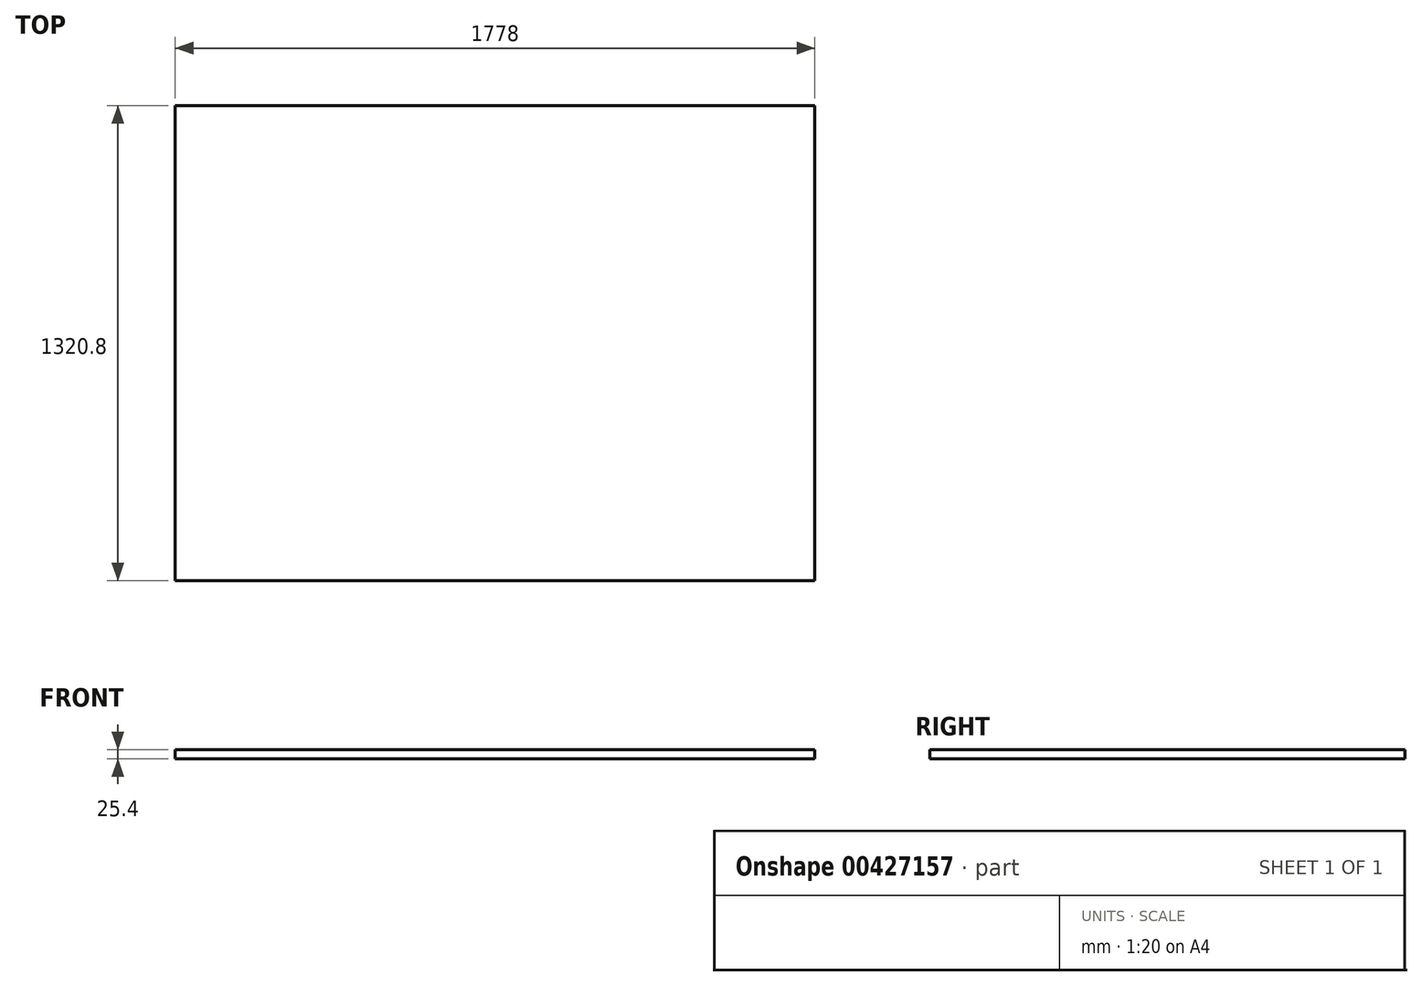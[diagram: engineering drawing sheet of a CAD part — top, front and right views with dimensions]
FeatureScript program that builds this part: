
annotation { "Feature Type Name" : "Feature", "Feature Type Description" : "" }
export const myFeature = defineFeature(function(context is Context, id is Id, definition is map)
    precondition{}
    {
        {
            var Q0;
            Q0=qCreatedBy(makeId("Top.planeOp"),FACE);
            var sketch = newSketch(context, id + "F0", { "sketchPlane" : qUnion([Q0])});
            skLineSegment(sketch, "E0.bottom", {"start": v(889, 660.4) * mm, "end": v(-889, 660.4) * mm});
            skLineSegment(sketch, "E0.top", {"start": v(889, -660.4) * mm, "end": v(-889, -660.4) * mm});
            skLineSegment(sketch, "E0.left", {"start": v(889, 660.4) * mm, "end": v(889, -660.4) * mm});
            skLineSegment(sketch, "E0.right", {"start": v(-889, 660.4) * mm, "end": v(-889, -660.4) * mm});
            skPoint(sketch, "E0.middle", {"position": v(0, 0) * mm});
            skSolve(sketch);
        }
        {
            var Q0;
            Q0 = qSketchRegion(id + "F0", true);
            extrude(context, id + "F1", {"entities" : qUnion([Q0]), "depth" : 25.4 * mm});
        }
    });
